# Revit family: L-street 40 Turbine GP
name_source: partatom
category: Осветительные приборы
revit_build: Autodesk Revit 2017 (Build: 20160225_1515(x64)
units: mm (PartAtom-declared; Revit-internal decimal feet)

## family parameters
Всегда вертикально = Да
Источник света = Да
На основе рабочей плоскости = Нет
Общий = Нет
При загрузке вырезать с полостями = Нет
Размер круглого соединителя = Использовать диаметр
Тип детали = Нормальный
Точка расчета площади = Нет

## types (4) — shared parameters
Изготовитель = LEDEL
Классификация нагрузок = Освещение
Комментарии к типоразмеру = Уличные
Светофильтр = 16777215
Смещение цветовой температуры при затухании лампы = <Нет>
Угол наклона = 90.00°

## per-type parameters (varying)
| type | Артикул | Полная установленная мощность | Файл фотометрической сетки |
| L-industry 40 Turbine GP 5.0K Охрана | 424211499751731 | 15 В·А | L-street 40 Turbine GP Security.ies |
| L-industry 40 Turbine GP 5.0K Тревога | 424211499751731 | 100 В·А | L-street 40 Turbine GP Alert.ies |
| L-industry 40 Turbine GP 4.0K Тревога | 424211499741731 | 100 В·А | L-street 40 Turbine GP Alert.ies |
| L-industry 40 Turbine GP 4.0K Охрана | 424211499741731 | 15 В·А | L-street 40 Turbine GP Security.ies |
